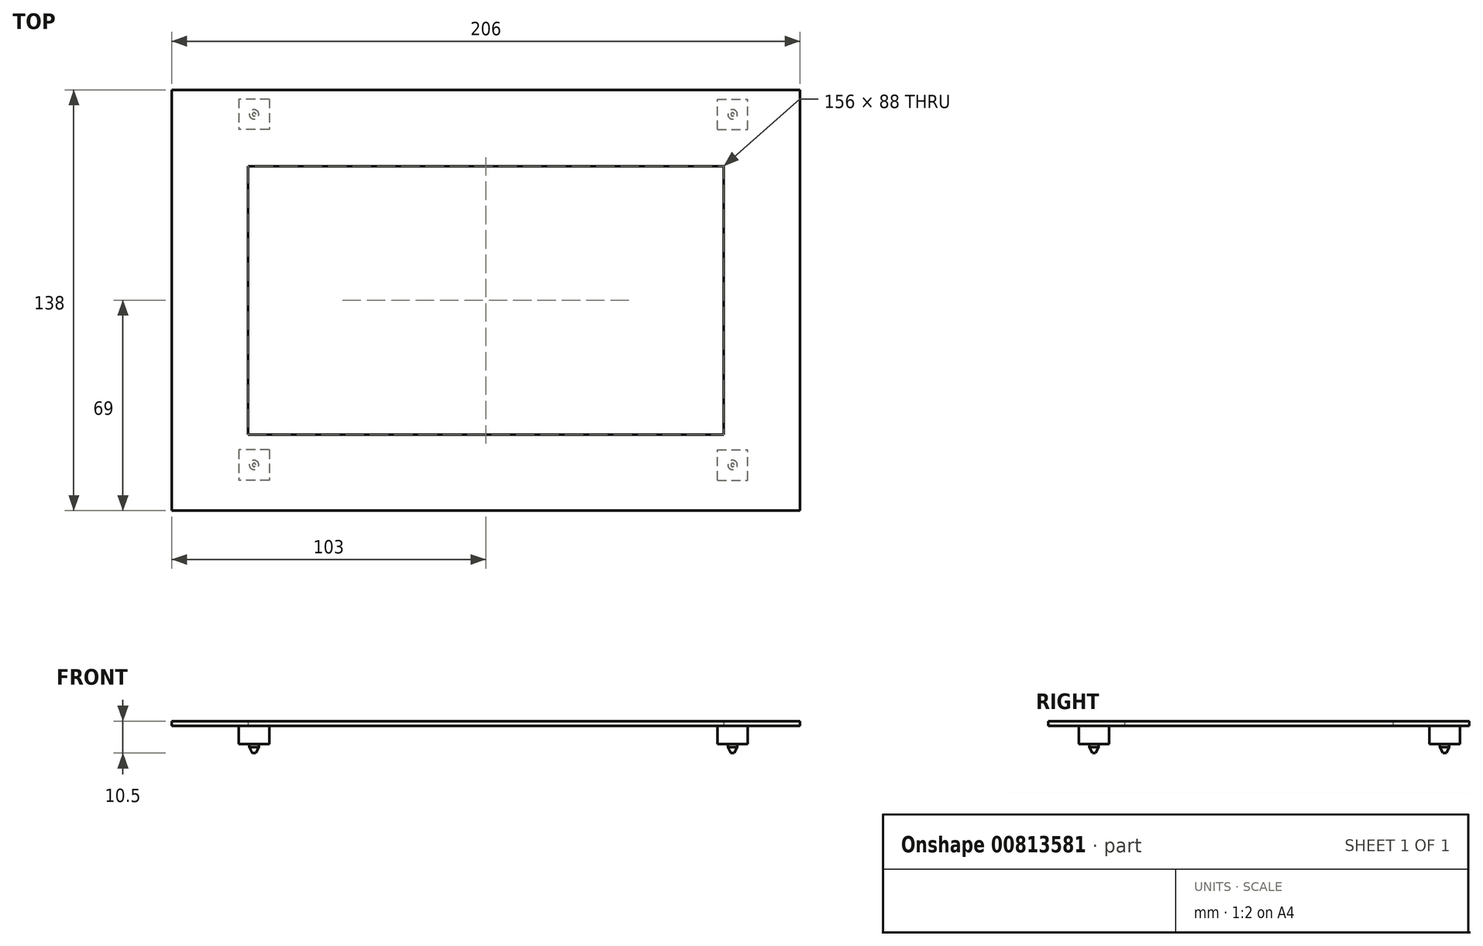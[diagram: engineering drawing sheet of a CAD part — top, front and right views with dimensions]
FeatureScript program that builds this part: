
annotation { "Feature Type Name" : "Feature", "Feature Type Description" : "" }
export const myFeature = defineFeature(function(context is Context, id is Id, definition is map)
    precondition{}
    {
        {
            var Q0;
            Q0=qCreatedBy(makeId("Top.planeOp"),FACE);
            var sketch = newSketch(context, id + "F0", { "sketchPlane" : qUnion([Q0])});
            skLineSegment(sketch, "E0.bottom", {"start": v(-103, 69) * mm, "end": v(103, 69) * mm});
            skLineSegment(sketch, "E0.top", {"start": v(-103, -69) * mm, "end": v(103, -69) * mm});
            skLineSegment(sketch, "E0.left", {"start": v(-103, 69) * mm, "end": v(-103, -69) * mm});
            skLineSegment(sketch, "E0.right", {"start": v(103, 69) * mm, "end": v(103, -69) * mm});
            skPoint(sketch, "E0.middle", {"position": v(0, 0) * mm});
            skLineSegment(sketch, "E1.bottom", {"start": v(-78, 44) * mm, "end": v(78, 44) * mm});
            skLineSegment(sketch, "E1.top", {"start": v(-78, -44) * mm, "end": v(78, -44) * mm});
            skLineSegment(sketch, "E1.left", {"start": v(-78, 44) * mm, "end": v(-78, -44) * mm});
            skLineSegment(sketch, "E1.right", {"start": v(78, 44) * mm, "end": v(78, -44) * mm});
            skSolve(sketch);
        }
        {
            var Q0;
            Q0 = qSketchRegion(id + "F0", true);
            extrude(context, id + "F1", {"entities" : qUnion([Q0]), "depth" : 1.5 * mm, "offsetDistance" : 25 * mm});
        }
        {
            var Q0;
            Q0=makeQuery(id+"F1.opExtrude","CAP_FACE",FACE,{"disambiguationData":[OSD([sQuery(id+"F0.wireOp",EDGE,"E0.bottom"),sQuery(id+"F0.wireOp",EDGE,"E0.top"),sQuery(id+"F0.wireOp",EDGE,"E0.left"),sQuery(id+"F0.wireOp",EDGE,"E0.right"),sQuery(id+"F0.wireOp",EDGE,"E1.bottom"),sQuery(id+"F0.wireOp",EDGE,"E1.top"),sQuery(id+"F0.wireOp",EDGE,"E1.left"),sQuery(id+"F0.wireOp",EDGE,"E1.right")])],"isStart":true});
            var sketch = newSketch(context, id + "F2", { "sketchPlane" : qUnion([Q0])});
            skLineSegment(sketch, "E2.bottom", {"start": v(-71, 49) * mm, "end": v(-81, 49) * mm});
            skLineSegment(sketch, "E2.top", {"start": v(-71, 59) * mm, "end": v(-81, 59) * mm});
            skLineSegment(sketch, "E2.left", {"start": v(-71, 49) * mm, "end": v(-71, 59) * mm});
            skLineSegment(sketch, "E2.right", {"start": v(-81, 49) * mm, "end": v(-81, 59) * mm});
            skPoint(sketch, "E2.middle", {"position": v(-76, 54) * mm});
            skLineSegment(sketch, "E3.bottom", {"start": v(75.9, 59) * mm, "end": v(85.9, 59) * mm});
            skLineSegment(sketch, "E3.top", {"start": v(75.9, 49) * mm, "end": v(85.9, 49) * mm});
            skLineSegment(sketch, "E3.left", {"start": v(75.9, 59) * mm, "end": v(75.9, 49) * mm});
            skLineSegment(sketch, "E3.right", {"start": v(85.9, 59) * mm, "end": v(85.9, 49) * mm});
            skPoint(sketch, "E3.middle", {"position": v(80.9, 54) * mm});
            skLineSegment(sketch, "E4.bottom", {"start": v(75.9, -55.96) * mm, "end": v(85.9, -55.96) * mm});
            skLineSegment(sketch, "E4.top", {"start": v(75.9, -65.96) * mm, "end": v(85.9, -65.96) * mm});
            skLineSegment(sketch, "E4.left", {"start": v(75.9, -55.96) * mm, "end": v(75.9, -65.96) * mm});
            skLineSegment(sketch, "E4.right", {"start": v(85.9, -55.96) * mm, "end": v(85.9, -65.96) * mm});
            skPoint(sketch, "E4.middle", {"position": v(80.9, -60.96) * mm});
            skLineSegment(sketch, "E5.bottom", {"start": v(-71, -65.96) * mm, "end": v(-81, -65.96) * mm});
            skLineSegment(sketch, "E5.top", {"start": v(-71, -55.96) * mm, "end": v(-81, -55.96) * mm});
            skLineSegment(sketch, "E5.left", {"start": v(-71, -65.96) * mm, "end": v(-71, -55.96) * mm});
            skLineSegment(sketch, "E5.right", {"start": v(-81, -65.96) * mm, "end": v(-81, -55.96) * mm});
            skPoint(sketch, "E5.middle", {"position": v(-76, -60.96) * mm});
            skCircle(sketch, "E6", {"center": v(-76, -60.96) * mm, "radius": 1.55 * mm});
            skCircle(sketch, "E7", {"center": v(-76, 54) * mm, "radius": 1.55 * mm});
            skCircle(sketch, "E8", {"center": v(80.9, 54) * mm, "radius": 1.55 * mm});
            skCircle(sketch, "E9", {"center": v(80.9, -60.96) * mm, "radius": 1.55 * mm});
            skSolve(sketch);
        }
        {
            var Q0;
            Q0 = qSketchRegion(id + "F2", true);
            var Q1;
            Q1=makeQuery(id+"F2.imprint","IMPRINT",FACE,{"disambiguationData":[TD([[makeQuery(id+"F2.imprint","IMPRINT",EDGE,{"derivedFrom":sQuery(id+"F2.wireOp",EDGE,"E7")}),1.0]])]});
            var Q2;
            Q2=makeQuery(id+"F2.imprint","IMPRINT",FACE,{"disambiguationData":[TD([[makeQuery(id+"F2.imprint","IMPRINT",EDGE,{"derivedFrom":sQuery(id+"F2.wireOp",EDGE,"E6")}),1.0]])]});
            var Q3;
            Q3=makeQuery(id+"F2.imprint","IMPRINT",FACE,{"disambiguationData":[TD([[makeQuery(id+"F2.imprint","IMPRINT",EDGE,{"derivedFrom":sQuery(id+"F2.wireOp",EDGE,"E9")}),1.0]])]});
            var Q4;
            Q4=makeQuery(id+"F2.imprint","IMPRINT",FACE,{"disambiguationData":[TD([[makeQuery(id+"F2.imprint","IMPRINT",EDGE,{"derivedFrom":sQuery(id+"F2.wireOp",EDGE,"E8")}),1.0]])]});
            extrude(context, id + "F3", {"entities" : qUnion([Q0, Q1, Q2, Q3, Q4]), "operationType" : NewBodyOperationType.ADD, "depth" : 6 * mm, "offsetDistance" : 25 * mm});
        }
        {
            var Q0;
            Q0=makeQuery(id+"F2.imprint","IMPRINT",FACE,{"disambiguationData":[TD([[makeQuery(id+"F2.imprint","IMPRINT",EDGE,{"derivedFrom":sQuery(id+"F2.wireOp",EDGE,"E7")}),1.0]])]});
            var Q1;
            Q1=makeQuery(id+"F2.imprint","IMPRINT",FACE,{"disambiguationData":[TD([[makeQuery(id+"F2.imprint","IMPRINT",EDGE,{"derivedFrom":sQuery(id+"F2.wireOp",EDGE,"E6")}),1.0]])]});
            var Q2;
            Q2=makeQuery(id+"F2.imprint","IMPRINT",FACE,{"disambiguationData":[TD([[makeQuery(id+"F2.imprint","IMPRINT",EDGE,{"derivedFrom":sQuery(id+"F2.wireOp",EDGE,"E9")}),1.0]])]});
            var Q3;
            Q3=makeQuery(id+"F2.imprint","IMPRINT",FACE,{"disambiguationData":[TD([[makeQuery(id+"F2.imprint","IMPRINT",EDGE,{"derivedFrom":sQuery(id+"F2.wireOp",EDGE,"E8")}),1.0]])]});
            extrude(context, id + "F4", {"entities" : qUnion([Q0, Q1, Q2, Q3]), "operationType" : NewBodyOperationType.ADD, "depth" : 9 * mm, "offsetDistance" : 25 * mm});
        }
        {
            var Q0;
            Q0=makeQuery(id+"F4.opExtrude","CAP_EDGE",EDGE,{"disambiguationData":[OSD([sQuery(id+"F2.wireOp",EDGE,"E7")])],"isStart":false});
            var Q1;
            Q1=makeQuery(id+"F4.opExtrude","CAP_EDGE",EDGE,{"disambiguationData":[OSD([sQuery(id+"F2.wireOp",EDGE,"E6")])],"isStart":false});
            var Q2;
            Q2=makeQuery(id+"F4.opExtrude","CAP_EDGE",EDGE,{"disambiguationData":[OSD([sQuery(id+"F2.wireOp",EDGE,"E8")])],"isStart":false});
            var Q3;
            Q3=makeQuery(id+"F4.opExtrude","CAP_EDGE",EDGE,{"disambiguationData":[OSD([sQuery(id+"F2.wireOp",EDGE,"E9")])],"isStart":false});
            chamfer(context, id + "F5", {"entities" : qUnion([Q0, Q1, Q2, Q3]), "chamferType" : ChamferType.TWO_OFFSETS, "width1" : 1 * mm, "oppositeDirection" : false, "width2" : 2 * mm, "tangentPropagation" : true});
        }
    });
